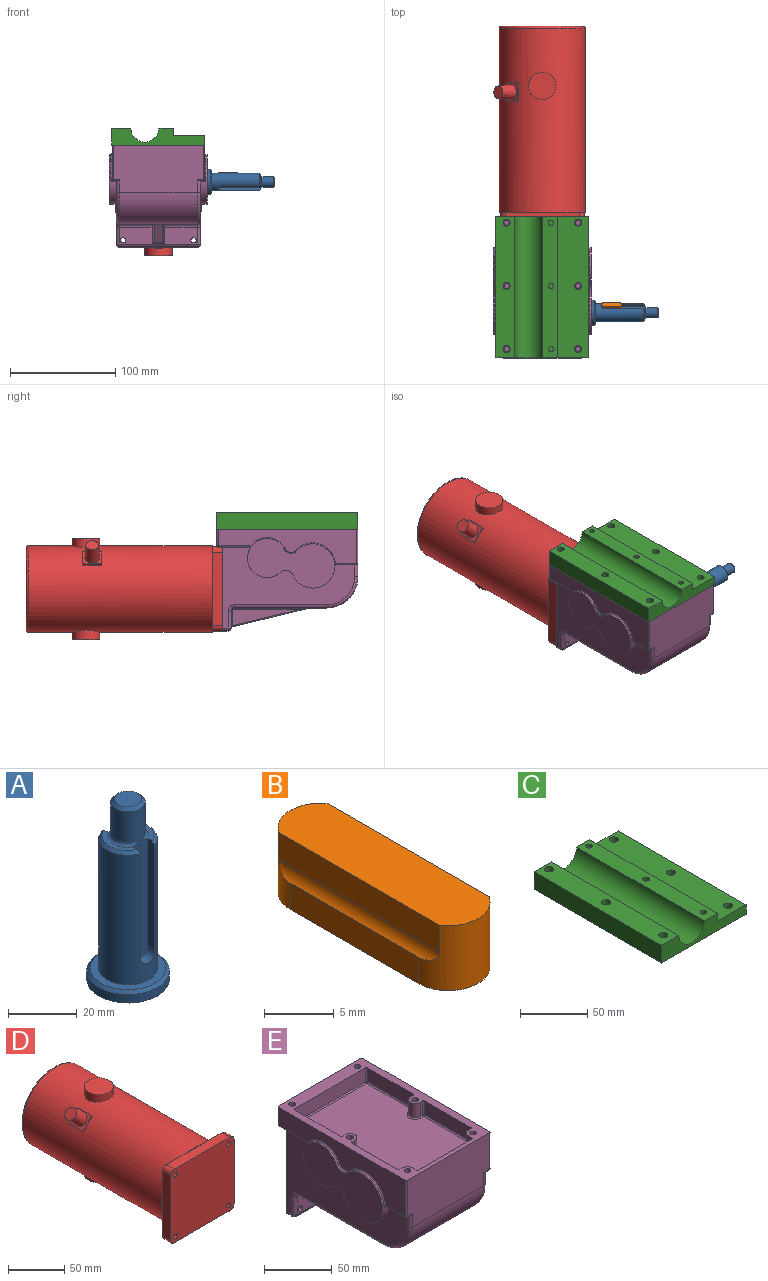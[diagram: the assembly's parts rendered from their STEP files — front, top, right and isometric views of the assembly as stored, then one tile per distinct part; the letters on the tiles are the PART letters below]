
ASSEMBLY  parts=5 mates=4
PART A: 21 faces, bbox 24x24x64 mm
  f0: plane 13.75x4.5mm, normal (0,0,1), area 22.7mm2, adj f4,f14,f17,f20
  f1: plane 13.75x4.5mm, normal (0,0,1), area 22.7mm2, adj f3,f12,f16,f20
  f2: cylinder r=8.5mm len=46mm, axis (0,0,1), area 1974.2mm2, adj f3,f4,f7,f12,f13,f14,f16,f17
  f3: cone r=7.5mm half-angle=45deg, axis (0,0,-1), area 26.8mm2, adj f1,f2,f12,f16
  f4: cone r=7.5mm half-angle=45deg, axis (0,0,-1), area 26.8mm2, adj f0,f2,f14,f17
  f5: plane 24x24mm, normal (0,0,-1), area 452.4mm2, adj f6
  f6: cylinder r=12mm len=24mm, axis (0,0,1), area 226.2mm2, adj f5,f10
  f7: plane 22x22mm, normal (0,0,1), area 153.2mm2, adj f2,f10
  f8: cylinder r=4.98mm len=11mm, axis (0,0,1), area 344.2mm2, adj f11,f20
  f9: plane 7.96x7.96mm, normal (0,0,1), area 49.8mm2, adj f11
  f10: cone r=11mm half-angle=45deg, axis (0,0,-1), area 102.2mm2, adj f6,f7
  f11: cone r=3.98mm half-angle=45deg, axis (0,0,-1), area 39.8mm2, adj f8,f9
  f12: plane 38.04x2.98mm, normal (1,0,0), area 111.7mm2, adj f1,f2,f3,f13,f15,f20
  f13: cylinder r=3mm len=6mm, axis (0,-1,0), area 30.4mm2, adj f2,f12,f14,f15
  f14: plane 38.04x2.98mm, normal (-1,0,0), area 111.7mm2, adj f0,f2,f4,f13,f15,f20
  f15: plane 41.8x6mm, normal (0,1,0), area 244.4mm2, adj f12,f13,f14,f20
  f16: plane 38.04x2.98mm, normal (1,0,0), area 111.7mm2, adj f1,f2,f3,f18,f19,f20
  f17: plane 38.04x2.98mm, normal (-1,0,0), area 111.7mm2, adj f0,f2,f4,f18,f19,f20
  f18: cylinder r=3mm len=6mm, axis (0,1,0), area 30.4mm2, adj f2,f16,f17,f19
  f19: plane 41.8x6mm, normal (0,-1,0), area 244.4mm2, adj f16,f17,f18,f20
  f20: torus R=5.98mm, axis (0,0,1), area 42.4mm2, adj f0,f1,f8,f12,f14,f15,f16,f17
PART B: 10 faces, bbox 6x19.1x5.7 mm
  f0: cylinder r=3mm len=6mm, axis (0,0,-1), area 42.5mm2, adj f1,f3,f4,f5,f6,f7,f8,f9
  f1: plane 13.05x2.32mm, normal (1,0,0), area 30.2mm2, adj f0,f2,f5,f8
  f2: cylinder r=3mm len=6mm, axis (0,0,-1), area 42.5mm2, adj f1,f3,f4,f5,f6,f7,f8,f9
  f3: plane 19.05x5mm, normal (0,0,1), area 91.3mm2, adj f0,f2,f7,f9
  f4: plane 13.05x2.32mm, normal (-1,0,0), area 30.2mm2, adj f0,f2,f5,f6
  f5: plane 19.05x6mm, normal (0,0,-1), area 106.6mm2, adj f0,f1,f2,f4
  f6: cylinder r=1.27mm len=16.37mm, axis (0,-1,0), area 18.3mm2, adj f0,f2,f4,f7
  f7: plane 16.37x2.37mm, normal (-1,0,0), area 38.9mm2, adj f0,f2,f3,f6
  f8: cylinder r=1.27mm len=16.37mm, axis (0,-1,0), area 18.3mm2, adj f0,f1,f2,f9
  f9: plane 16.37x2.37mm, normal (1,0,0), area 38.9mm2, adj f0,f2,f3,f8
PART C: 22 faces, bbox 88.3x134x15.9 mm
  f0: plane 134x15.88mm, normal (-1,0,0), area 2127.2mm2, adj f1,f7,f8,f9
  f1: plane 134x88.25mm, normal (0,0,-1), area 11614mm2, adj f0,f2,f8,f9,f16,f17,f18,f19
  f2: plane 134x8.8mm, normal (1,0,0), area 1179.2mm2, adj f1,f3,f8,f9
  f3: plane 134x29.8mm, normal (0,0,1), area 3887.4mm2, adj f2,f4,f8,f9,f19,f20,f21
  f4: plane 134x7.08mm, normal (1,0,0), area 948mm2, adj f3,f5,f8,f9
  f5: plane 134x13.75mm, normal (0,0,1), area 1783.6mm2, adj f4,f6,f8,f9,f10,f12,f14
  f6: cylinder r=13.36mm len=134mm, axis (0,1,0), area 5520.3mm2, adj f5,f7,f8,f9
  f7: plane 134x18mm, normal (0,0,1), area 2306.2mm2, adj f0,f6,f8,f9,f16,f17,f18
  f8: plane 88.25x15.88mm, normal (0,-1,0), area 920.1mm2, adj f0,f1,f2,f3,f4,f5,f6,f7
  f9: plane 88.25x15.88mm, normal (0,1,0), area 920.1mm2, adj f0,f1,f2,f3,f4,f5,f6,f7
  f10: cylinder r=2.5mm len=7.08mm, axis (0,0,-1), area 111.1mm2, adj f5,f11
  f11: plane 5x5mm, normal (0,0,1), area 19.6mm2, adj f10
  f12: cylinder r=2.5mm len=7.08mm, axis (0,0,-1), area 111.1mm2, adj f5,f13
  f13: plane 5x5mm, normal (0,0,1), area 19.6mm2, adj f12
  f14: cylinder r=2.5mm len=7.08mm, axis (0,0,-1), area 111.1mm2, adj f5,f15
  f15: plane 5x5mm, normal (0,0,1), area 19.6mm2, adj f14
  f16: cylinder r=3.35mm len=15.88mm, axis (0,0,1), area 334.1mm2, adj f1,f7
  f17: cylinder r=3.35mm len=15.88mm, axis (0,0,1), area 334.1mm2, adj f1,f7
  f18: cylinder r=3.35mm len=15.88mm, axis (0,0,1), area 334.1mm2, adj f1,f7
  f19: cylinder r=3.35mm len=8.8mm, axis (0,0,1), area 185.2mm2, adj f1,f3
  f20: cylinder r=3.35mm len=8.8mm, axis (0,0,1), area 185.2mm2, adj f1,f3
  f21: cylinder r=3.35mm len=8.8mm, axis (0,0,1), area 185.2mm2, adj f1,f3
PART D: 35 faces, bbox 90.4x187x96 mm
  f0: cylinder r=41mm len=175mm, axis (0,-1,0), area 43717.7mm2, adj f1,f2,f3,f12,f14,f15,f16,f18
  f1: plane 31x31mm, normal (0,1,0), area 266.8mm2, adj f0,f4,f7,f11,f33
  f2: plane 31x31mm, normal (0,1,0), area 266.8mm2, adj f0,f6,f8,f11,f32
  f3: plane 31x31mm, normal (0,1,0), area 266.8mm2, adj f0,f5,f6,f9,f31
  f4: plane 70x10mm, normal (-1,0,0), area 700mm2, adj f1,f12,f13,f16,f30,f33
  f5: plane 70x10mm, normal (0,0,-1), area 700mm2, adj f3,f12,f13,f18,f30,f31
  f6: plane 70x10mm, normal (1,0,0), area 700mm2, adj f2,f3,f13,f15,f31,f32
  f7: cylinder r=2.5mm len=10mm, axis (0,-1,0), area 157.1mm2, adj f1,f13
  f8: cylinder r=2.5mm len=10mm, axis (0,-1,0), area 157.1mm2, adj f2,f13
  f9: cylinder r=2.5mm len=10mm, axis (0,-1,0), area 157.1mm2, adj f3,f13
  f10: cylinder r=2.5mm len=10mm, axis (0,-1,0), area 157.1mm2, adj f12,f13
  f11: plane 70x10mm, normal (0,0,1), area 700mm2, adj f1,f2,f13,f14,f32,f33
  f12: plane 31x31mm, normal (0,1,0), area 266.8mm2, adj f0,f4,f5,f10,f30
  f13: plane 80x80mm, normal (0,-1,0), area 6300mm2, adj f4,f5,f6,f7,f8,f9,f10,f11
  f14: plane 18x1mm, normal (0,-1,0), area 12mm2, adj f0,f11
  f15: plane 18x1mm, normal (0,-1,0), area 12mm2, adj f0,f6
  f16: plane 18x1mm, normal (0,-1,0), area 12mm2, adj f0,f4
  f17: plane 78x78mm, normal (0,1,0), area 4778.4mm2, adj f34
  f18: plane 18x1mm, normal (0,-1,0), area 12mm2, adj f0,f5
  f19: plane 26x26mm, normal (0,0,1), area 530.9mm2, adj f20
  f20: cylinder r=13mm len=26mm, axis (0,0,-1), area 657.5mm2, adj f0,f19
  f21: cylinder r=13mm len=26mm, axis (0,0,-1), area 657.6mm2, adj f0,f22
  f22: plane 26x26mm, normal (0,0,-1), area 530.9mm2, adj f21
  f23: plane 18x1.26mm, normal (0.71,0,0.71), area 32.2mm2, adj f0,f25,f26,f27
  f24: plane 18x1.26mm, normal (-0.71,0,-0.71), area 32.2mm2, adj f0,f25,f26,f27
  f25: plane 12.58x12.58mm, normal (0,1,0), area 20.2mm2, adj f0,f23,f24,f27
  f26: plane 12.58x12.58mm, normal (0,-1,0), area 20.2mm2, adj f0,f23,f24,f27
  f27: plane 18x11.31mm, normal (-0.71,0,0.71), area 134.1mm2, adj f23,f24,f25,f26,f28
  f28: cone r=7mm half-angle=3deg, axis (0.71,0,-0.71), area 701.1mm2, adj f27,f29
  f29: plane 12.22x8.64mm, normal (-0.71,0,0.71), area 117.2mm2, adj f28
  f30: cylinder r=5mm len=10mm, axis (0,-1,0), area 78.5mm2, adj f4,f5,f12,f13
  f31: cylinder r=5mm len=10mm, axis (0,1,0), area 78.5mm2, adj f3,f5,f6,f13
  f32: cylinder r=5mm len=10mm, axis (0,-1,0), area 78.5mm2, adj f2,f6,f11,f13
  f33: cylinder r=5mm len=10mm, axis (0,1,0), area 78.5mm2, adj f1,f4,f11,f13
  f34: torus R=39mm, axis (0,1,0), area 795mm2, adj f0,f17
PART E: 163 faces, bbox 93x136.5x97 mm
  f0: cylinder r=3mm len=31mm, axis (1,0,0), area 146.1mm2, adj f3,f10,f45,f150
  f1: plane 134x88mm, normal (0,0,1), area 2921.3mm2, adj f2,f24,f25,f26,f48,f57,f64,f69
  f2: plane 86x45mm, normal (0,-1,0), area 3726mm2, adj f1,f31,f32,f34,f48,f49,f56,f57
  f3: plane 87.5x74mm, normal (0,0,-1), area 5616.9mm2, adj f0,f31,f35,f41,f42,f149,f151,f154
  f4: plane 80x80mm, normal (0,1,0), area 6317.6mm2, adj f5,f6,f7,f8,f9,f11,f13,f23
  f5: plane 125.5x77mm, normal (1,0,0), area 4068.3mm2, adj f4,f19,f20,f21,f22,f23,f32,f33
  f6: plane 125.5x77mm, normal (-1,0,0), area 4068.3mm2, adj f4,f15,f16,f17,f18,f23,f34,f38
  f7: plane 74x5mm, normal (0,0,-1), area 370mm2, adj f4,f37,f43,f44
  f8: cylinder r=2.5mm len=8mm, axis (0,1,0), area 125.7mm2, adj f4,f10
  f9: cylinder r=2.5mm len=8mm, axis (0,1,0), area 125.7mm2, adj f4,f10
  f10: plane 74x16mm, normal (0,-1,0), area 957mm2, adj f0,f8,f9,f36,f42,f43,f47,f152
  f11: cylinder r=2.5mm len=6mm, axis (0,1,0), area 94.2mm2, adj f4,f12
  f12: plane 5x5mm, normal (0,1,0), area 19.6mm2, adj f11
  f13: cylinder r=2.5mm len=6mm, axis (0,1,0), area 94.2mm2, adj f4,f14
  f14: plane 5x5mm, normal (0,1,0), area 19.6mm2, adj f13
  f15: plane 20x3.76mm, normal (0,0,-1), area 60.5mm2, adj f6,f34,f49,f51,f52
  f16: cylinder r=21mm len=42mm, axis (-1,0,0), area 449.8mm2, adj f6,f17,f27,f28,f52,f53,f54
  f17: cylinder r=7.11mm len=11.42mm, axis (-1,0,0), area 88.9mm2, adj f6,f16,f18,f27
  f18: cylinder r=18.5mm len=37mm, axis (-1,0,0), area 402.3mm2, adj f6,f17,f27,f28,f58,f59,f61
  f19: plane 20x3.76mm, normal (0,0,-1), area 60.5mm2, adj f5,f32,f56,f62,f63
  f20: cylinder r=21mm len=42mm, axis (-1,0,0), area 449.8mm2, adj f5,f21,f29,f30,f62,f66,f68
  f21: cylinder r=7.11mm len=11.42mm, axis (-1,0,0), area 88.9mm2, adj f5,f20,f22,f30
  f22: cylinder r=18.5mm len=37mm, axis (-1,0,0), area 402.3mm2, adj f5,f21,f29,f30,f73,f75,f76
  f23: plane 86x29.51mm, normal (0,0,-1), area 537.1mm2, adj f4,f5,f6,f59,f65,f70,f74,f76
  f24: plane 86x16mm, normal (0,1,0), area 1376mm2, adj f1,f64,f69,f70
  f25: plane 132x33mm, normal (1,0,0), area 2354mm2, adj f1,f57,f63,f68,f69,f71,f73,f74
  f26: plane 132x33mm, normal (-1,0,0), area 2354mm2, adj f1,f48,f51,f54,f55,f58,f64,f65
  f27: plane 82.96x47mm, normal (-1,0,0), area 2565.2mm2, adj f16,f17,f18,f28
  f28: cylinder r=7.11mm len=11.55mm, axis (-1,0,0), area 20.5mm2, adj f16,f18,f27,f55
  f29: cylinder r=7.11mm len=11.55mm, axis (-1,0,0), area 20.5mm2, adj f20,f22,f30,f71
  f30: plane 82.96x47mm, normal (1,0,0), area 2565.2mm2, adj f20,f21,f22,f29
  f31: cylinder r=30mm len=74mm, axis (1,0,0), area 3487.2mm2, adj f2,f3,f33,f38
  f32: cylinder r=3mm len=12mm, axis (0,0,1), area 53.1mm2, adj f2,f5,f19,f33,f56
  f33: torus R=27mm, axis (1,0,0), area 214mm2, adj f5,f31,f32,f35
  f34: cylinder r=3mm len=12mm, axis (0,0,-1), area 53.1mm2, adj f2,f6,f15,f38,f49
  f35: cylinder r=3mm len=87.5mm, axis (0,-1,0), area 412.3mm2, adj f3,f5,f33,f39
  f36: cylinder r=3mm len=16mm, axis (0,0,-1), area 75.4mm2, adj f5,f10,f39,f40
  f37: cylinder r=3mm len=5mm, axis (0,-1,0), area 23.6mm2, adj f4,f5,f7,f40
  f38: torus R=27mm, axis (1,0,0), area 214mm2, adj f6,f31,f34,f41
  f39: torus R=6mm, axis (1,0,0), area 30.3mm2, adj f5,f35,f36,f42
  f40: sphere r=3mm, area 14.1mm2, adj f36,f37,f43
  f41: cylinder r=3mm len=87.5mm, axis (0,1,0), area 412.3mm2, adj f3,f6,f38,f45
  f42: cylinder r=3mm len=31mm, axis (1,0,0), area 146.1mm2, adj f3,f10,f39,f160
  f43: cylinder r=3mm len=74mm, axis (-1,0,0), area 348.7mm2, adj f7,f10,f40,f46
  f44: cylinder r=3mm len=5mm, axis (0,1,0), area 23.6mm2, adj f4,f6,f7,f46
  f45: torus R=6mm, axis (1,0,0), area 30.3mm2, adj f0,f6,f41,f47
  f46: sphere r=3mm, area 14.1mm2, adj f43,f44,f47
  f47: cylinder r=3mm len=16mm, axis (0,0,1), area 75.4mm2, adj f6,f10,f45,f46
  f48: cylinder r=1mm len=33mm, axis (0,0,-1), area 51.8mm2, adj f1,f2,f26,f50
  f49: cylinder r=1mm len=6mm, axis (-1,0,0), area 7.7mm2, adj f2,f15,f34,f50
  f50: sphere r=1mm, area 1.6mm2, adj f48,f49,f51
  f51: cylinder r=1mm len=20.09mm, axis (0,1,0), area 31.5mm2, adj f15,f26,f50,f53
  f52: cylinder r=1mm len=3mm, axis (-1,0,0), area 4.7mm2, adj f6,f15,f16,f53
  f53: bspline ~2.45x2.23mm, area 3.3mm2, adj f16,f51,f52,f54
  f54: torus R=22mm, axis (1,0,0), area 77.3mm2, adj f16,f26,f53,f55
  f55: torus R=6.11mm, axis (1,0,0), area 20.4mm2, adj f26,f28,f54,f58
  f56: cylinder r=1mm len=6mm, axis (-1,0,0), area 7.7mm2, adj f2,f19,f32,f60
  f57: cylinder r=1mm len=33mm, axis (0,0,1), area 51.8mm2, adj f1,f2,f25,f60
  f58: torus R=19.5mm, axis (1,0,0), area 60.5mm2, adj f18,f26,f55,f61
  f59: cylinder r=1mm len=3mm, axis (-1,0,0), area 6.2mm2, adj f6,f18,f23,f61
  f60: sphere r=1mm, area 1.6mm2, adj f56,f57,f63
  f61: bspline ~2.77x2.49mm, area 4.3mm2, adj f18,f58,f59,f65
  f62: cylinder r=1mm len=3mm, axis (-1,0,0), area 4.7mm2, adj f5,f19,f20,f66
  f63: cylinder r=1mm len=20.09mm, axis (0,-1,0), area 31.5mm2, adj f19,f25,f60,f66
  f64: cylinder r=1mm len=16mm, axis (0,0,1), area 25.1mm2, adj f1,f24,f26,f67
  f65: cylinder r=1mm len=30.79mm, axis (0,1,0), area 47.1mm2, adj f23,f26,f61,f67
  f66: bspline ~2.34x2.34mm, area 3.3mm2, adj f20,f62,f63,f68
  f67: sphere r=1mm, area 1.6mm2, adj f64,f65,f70
  f68: torus R=22mm, axis (1,0,0), area 77.3mm2, adj f20,f25,f66,f71
  f69: cylinder r=1mm len=16mm, axis (0,0,-1), area 25.1mm2, adj f1,f24,f25,f72
  f70: cylinder r=1mm len=86mm, axis (-1,0,0), area 135.1mm2, adj f23,f24,f67,f72
  f71: torus R=6.11mm, axis (1,0,0), area 20.4mm2, adj f25,f29,f68,f73
  f72: sphere r=1mm, area 1.6mm2, adj f69,f70,f74
  f73: torus R=19.5mm, axis (1,0,0), area 60.5mm2, adj f22,f25,f71,f75
  f74: cylinder r=1mm len=30.79mm, axis (0,-1,0), area 47.1mm2, adj f23,f25,f72,f75
  f75: bspline ~2.7x2.4mm, area 4.3mm2, adj f22,f73,f74,f76
  f76: cylinder r=1mm len=3mm, axis (-1,0,0), area 6.2mm2, adj f5,f22,f23,f75
  f77: plane 56x12.5mm, normal (0,1,0), area 700mm2, adj f1,f139,f143,f145
  f78: plane 12.5x4mm, normal (-1,0,0), area 50mm2, adj f1,f79,f138,f139
  f79: cylinder r=5mm len=12.5mm, axis (0,0,1), area 98.2mm2, adj f1,f78,f80,f136
  f80: plane 12.5x3mm, normal (0,1,0), area 37.5mm2, adj f1,f79,f129,f134
  f81: plane 48x12.5mm, normal (-1,0,0), area 600mm2, adj f1,f123,f128,f129
  f82: plane 12.5x3mm, normal (0,-1,0), area 37.5mm2, adj f1,f83,f122,f123
  f83: cylinder r=5mm len=12.5mm, axis (0,0,1), area 196.3mm2, adj f1,f82,f84,f120
  f84: plane 12.5x3mm, normal (0,1,0), area 37.5mm2, adj f1,f83,f113,f118
  f85: plane 47.5x12.5mm, normal (-1,0,0), area 593.8mm2, adj f1,f108,f112,f113
  f86: plane 74x12.5mm, normal (0,-1,0), area 925mm2, adj f1,f108,f110,f111
  f87: plane 47.5x12.5mm, normal (1,0,0), area 593.8mm2, adj f1,f110,f116,f117
  f88: plane 12.5x3mm, normal (0,1,0), area 37.5mm2, adj f1,f89,f116,f121
  f89: cylinder r=5mm len=12.5mm, axis (0,0,1), area 196.3mm2, adj f1,f88,f90,f124
  f90: plane 12.5x3mm, normal (0,-1,0), area 37.5mm2, adj f1,f89,f126,f127
  f91: plane 48x12.5mm, normal (1,0,0), area 600mm2, adj f1,f126,f132,f133
  f92: plane 12.5x3mm, normal (0,1,0), area 37.5mm2, adj f1,f93,f132,f137
  f93: cylinder r=5mm len=12.5mm, axis (0,0,1), area 98.2mm2, adj f1,f92,f94,f140
  f94: plane 12.5x4mm, normal (1,0,0), area 50mm2, adj f1,f93,f142,f145
  f95: plane 117.5x74mm, normal (0,0,1), area 8345.4mm2, adj f111,f112,f117,f118,f120,f121,f122,f124
  f96: cylinder r=2.5mm len=13.5mm, axis (0,0,1), area 212.1mm2, adj f1,f97
  f97: plane 5x5mm, normal (0,0,1), area 19.6mm2, adj f96
  f98: cylinder r=2.5mm len=13.5mm, axis (0,0,1), area 212.1mm2, adj f1,f99
  f99: plane 5x5mm, normal (0,0,1), area 19.6mm2, adj f98
  f100: cylinder r=2.5mm len=13.5mm, axis (0,0,1), area 212.1mm2, adj f1,f101
  f101: plane 5x5mm, normal (0,0,1), area 19.6mm2, adj f100
  f102: cylinder r=2.5mm len=13.5mm, axis (0,0,1), area 212.1mm2, adj f1,f103
  f103: plane 5x5mm, normal (0,0,1), area 19.6mm2, adj f102
  f104: cylinder r=2.5mm len=13.5mm, axis (0,0,1), area 212.1mm2, adj f1,f105
  f105: plane 5x5mm, normal (0,0,1), area 19.6mm2, adj f104
  f106: cylinder r=2.5mm len=13.5mm, axis (0,0,1), area 212.1mm2, adj f1,f107
  f107: plane 5x5mm, normal (0,0,1), area 19.6mm2, adj f106
  f108: cylinder r=1mm len=12.5mm, axis (0,0,1), area 19.6mm2, adj f1,f85,f86,f109
  f109: sphere r=1mm, area 1.6mm2, adj f108,f111,f112
  f110: cylinder r=1mm len=12.5mm, axis (0,0,-1), area 19.6mm2, adj f1,f86,f87,f114
  f111: cylinder r=1mm len=74mm, axis (-1,0,0), area 116.2mm2, adj f86,f95,f109,f114
  f112: cylinder r=1mm len=47.5mm, axis (0,1,0), area 74.6mm2, adj f85,f95,f109,f115
  f113: cylinder r=1mm len=12.5mm, axis (0,0,1), area 19.6mm2, adj f1,f84,f85,f115
  f114: sphere r=1mm, area 1.6mm2, adj f110,f111,f117
  f115: sphere r=1mm, area 1.6mm2, adj f112,f113,f118
  f116: cylinder r=1mm len=12.5mm, axis (0,0,1), area 19.6mm2, adj f1,f87,f88,f119
  f117: cylinder r=1mm len=47.5mm, axis (0,-1,0), area 74.6mm2, adj f87,f95,f114,f119
  f118: cylinder r=1mm len=3mm, axis (1,0,0), area 4.7mm2, adj f84,f95,f115,f120
  f119: sphere r=1mm, area 1.6mm2, adj f116,f117,f121
  f120: torus R=6mm, axis (0,0,1), area 26.5mm2, adj f83,f95,f118,f122
  f121: cylinder r=1mm len=3mm, axis (1,0,0), area 4.7mm2, adj f88,f95,f119,f124
  f122: cylinder r=1mm len=3mm, axis (-1,0,0), area 4.7mm2, adj f82,f95,f120,f125
  f123: cylinder r=1mm len=12.5mm, axis (0,0,-1), area 19.6mm2, adj f1,f81,f82,f125
  f124: torus R=6mm, axis (0,0,1), area 26.5mm2, adj f89,f95,f121,f127
  f125: sphere r=1mm, area 1.6mm2, adj f122,f123,f128
  f126: cylinder r=1mm len=12.5mm, axis (0,0,-1), area 19.6mm2, adj f1,f90,f91,f130
  f127: cylinder r=1mm len=3mm, axis (-1,0,0), area 4.7mm2, adj f90,f95,f124,f130
  f128: cylinder r=1mm len=48mm, axis (0,1,0), area 75.4mm2, adj f81,f95,f125,f131
  f129: cylinder r=1mm len=12.5mm, axis (0,0,1), area 19.6mm2, adj f1,f80,f81,f131
  f130: sphere r=1mm, area 1.6mm2, adj f126,f127,f133
  f131: sphere r=1mm, area 1.6mm2, adj f128,f129,f134
  f132: cylinder r=1mm len=12.5mm, axis (0,0,1), area 19.6mm2, adj f1,f91,f92,f135
  f133: cylinder r=1mm len=48mm, axis (0,-1,0), area 75.4mm2, adj f91,f95,f130,f135
  f134: cylinder r=1mm len=3mm, axis (1,0,0), area 4.7mm2, adj f80,f95,f131,f136
  f135: sphere r=1mm, area 1.6mm2, adj f132,f133,f137
  f136: torus R=6mm, axis (0,0,1), area 13.2mm2, adj f79,f95,f134,f138
  f137: cylinder r=1mm len=3mm, axis (1,0,0), area 4.7mm2, adj f92,f95,f135,f140
  f138: cylinder r=1mm len=4mm, axis (0,1,0), area 6.3mm2, adj f78,f95,f136,f141
  f139: cylinder r=1mm len=12.5mm, axis (0,0,-1), area 19.6mm2, adj f1,f77,f78,f141
  f140: torus R=6mm, axis (0,0,1), area 13.2mm2, adj f93,f95,f137,f142
  f141: sphere r=1mm, area 1.6mm2, adj f138,f139,f143
  f142: cylinder r=1mm len=4mm, axis (0,-1,0), area 6.3mm2, adj f94,f95,f140,f144
  f143: cylinder r=1mm len=56mm, axis (1,0,0), area 88mm2, adj f77,f95,f141,f144
  f144: sphere r=1mm, area 1.6mm2, adj f142,f143,f145
  f145: cylinder r=1mm len=12.5mm, axis (0,0,1), area 19.6mm2, adj f1,f77,f94,f144
  f146: plane 65.55x15.73mm, normal (1,0,0), area 514.7mm2, adj f157,f159,f160,f162
  f147: plane 65.55x15.73mm, normal (-1,0,0), area 514.7mm2, adj f149,f150,f152,f153
  f148: plane 74.12x17.79mm, normal (0,-0.23,-0.97), area 609.8mm2, adj f153,f154,f158,f159
  f149: cylinder r=1mm len=63.55mm, axis (0,1,0), area 99.8mm2, adj f3,f147,f150,f151
  f150: torus R=2mm, axis (1,0,0), area 6.5mm2, adj f0,f147,f149,f152
  f151: bspline ~8.57x2mm, area 8.8mm2, adj f3,f149,f153,f154
  f152: cylinder r=1mm len=13.73mm, axis (0,0,-1), area 21.6mm2, adj f10,f147,f150,f155
  f153: cylinder r=1mm len=74.35mm, axis (0,0.97,-0.23), area 114.6mm2, adj f147,f148,f151,f155
  f154: cylinder r=1mm len=8mm, axis (1,0,0), area 1.9mm2, adj f3,f148,f151,f156
  f155: bspline ~2.14x2.06mm, area 3.2mm2, adj f10,f152,f153,f158
  f156: bspline ~8.57x2mm, area 8.8mm2, adj f3,f154,f157,f159
  f157: cylinder r=1mm len=63.55mm, axis (0,-1,0), area 99.8mm2, adj f3,f146,f156,f160
  f158: cylinder r=1mm len=8mm, axis (1,0,0), area 10.7mm2, adj f10,f148,f155,f161
  f159: cylinder r=1mm len=74.35mm, axis (0,-0.97,0.23), area 114.6mm2, adj f146,f148,f156,f161
  f160: torus R=2mm, axis (1,0,0), area 6.5mm2, adj f42,f146,f157,f162
  f161: bspline ~2.41x2.35mm, area 3.2mm2, adj f10,f158,f159,f162
  f162: cylinder r=1mm len=13.73mm, axis (0,0,1), area 21.6mm2, adj f10,f146,f160,f161
PLACE A rot(axis=(0.35,0.87,0.35),97.9deg) t=(46.5,-85.5,22)mm
PLACE B rot(axis=(-0.37,-0.37,-0.86),98.9deg) t=(66.03,-79.82,27.42)mm
PLACE C at identity
PLACE D t=(0,0,0.02)mm
PLACE E at identity fixed
MATE fastened B.f0 <-> A.f13  axis (0,-0.72,-0.69) through (59.5,-81.88,25.45)mm
MATE revolute A.f10 <-> E.f16  axis (-1,0,0) through (46.5,-85.5,22)mm
MATE fastened C.f20 <-> E.f79  axis (0,0,-1) through (34,-120,57)mm
MATE fastened D.f0 <-> E.f4  axis (0,-1,0) through (0,0,0.02)mm
